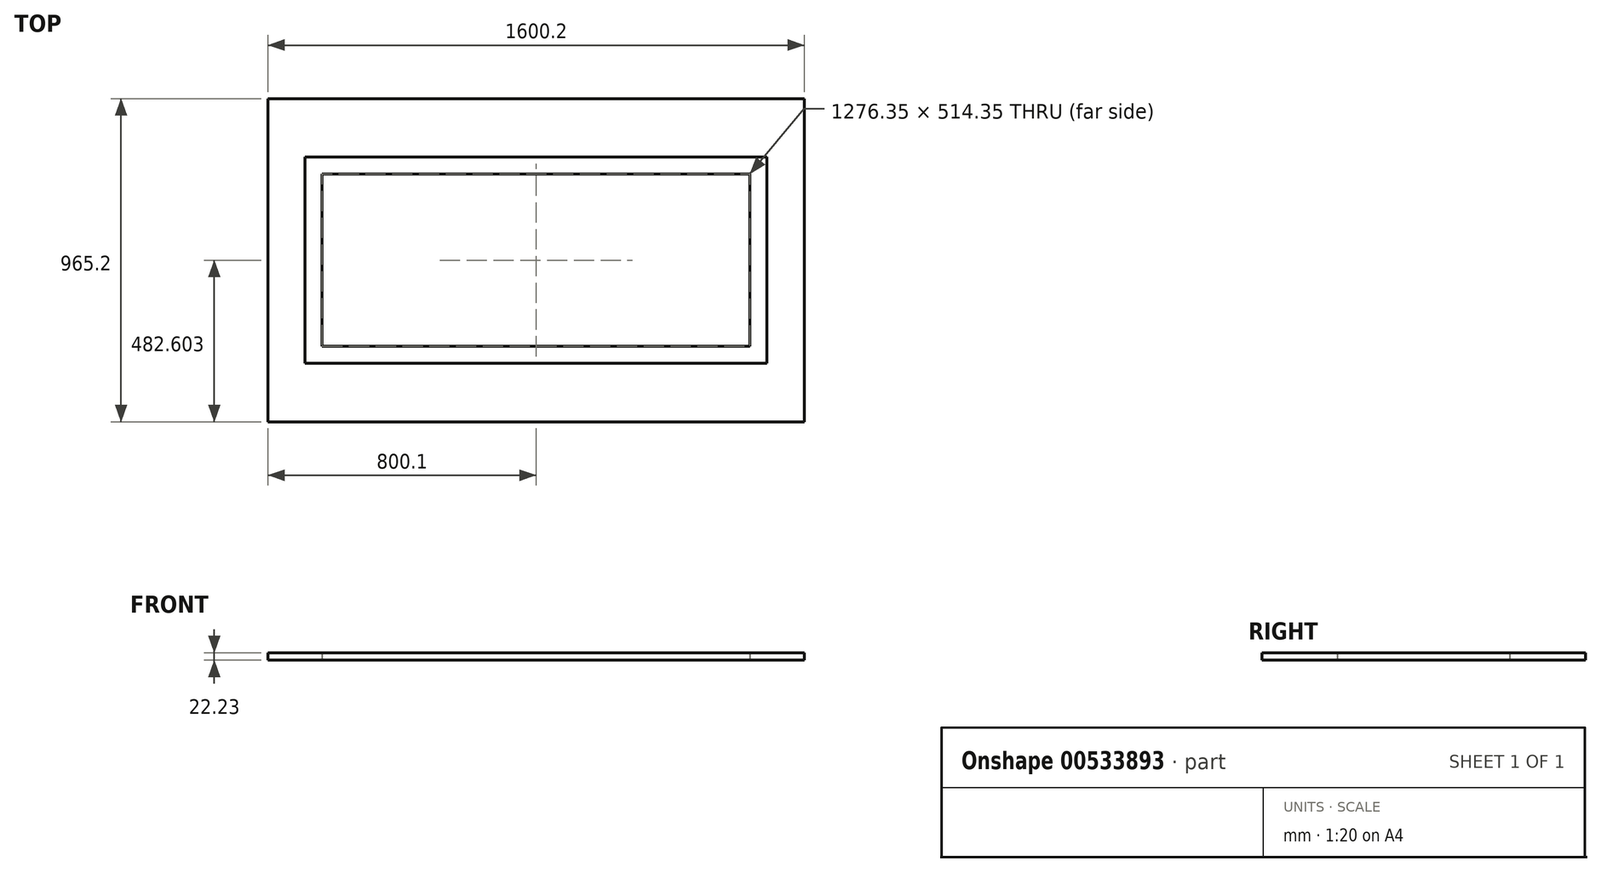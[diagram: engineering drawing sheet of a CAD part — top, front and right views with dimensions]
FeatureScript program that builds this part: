
annotation { "Feature Type Name" : "Feature", "Feature Type Description" : "" }
export const myFeature = defineFeature(function(context is Context, id is Id, definition is map)
    precondition{}
    {
        {
            var Q0;
            Q0=qCreatedBy(makeId("Top.planeOp"),FACE);
            var sketch = newSketch(context, id + "F0", { "sketchPlane" : qUnion([Q0])});
            skLineSegment(sketch, "E0", {"start": v(-545.3, 52.56) * mm, "end": v(-545.3, 1017.76) * mm});
            skLineSegment(sketch, "E1", {"start": v(-545.3, 1017.76) * mm, "end": v(1054.9, 1017.76) * mm});
            skLineSegment(sketch, "E2", {"start": v(-545.3, 52.56) * mm, "end": v(1054.9, 52.56) * mm});
            skLineSegment(sketch, "E3", {"start": v(1054.9, 1017.76) * mm, "end": v(1054.9, 52.56) * mm});
            skPoint(sketch, "E4.middle.positionSnap0", {"position": v(254.8, 1017.76) * mm});
            skPoint(sketch, "E4.middle.positionSnap1", {"position": v(-545.3, 535.16) * mm});
            skPoint(sketch, "E4.centerSnap0", {"position": v(254.8, 1017.76) * mm});
            skPoint(sketch, "E4.centerSnap1", {"position": v(-545.3, 535.16) * mm});
            skLineSegment(sketch, "E5.bottom", {"start": v(-434.18, 227.19) * mm, "end": v(943.77, 227.19) * mm});
            skLineSegment(sketch, "E5.top", {"start": v(-434.18, 843.14) * mm, "end": v(943.77, 843.14) * mm});
            skLineSegment(sketch, "E5.left", {"start": v(-434.18, 227.19) * mm, "end": v(-434.18, 843.14) * mm});
            skLineSegment(sketch, "E5.right", {"start": v(943.77, 227.19) * mm, "end": v(943.77, 843.14) * mm});
            skPoint(sketch, "E5.middle", {"position": v(254.8, 535.16) * mm});
            skLineSegment(sketch, "E6.bottom", {"start": v(-383.38, 277.99) * mm, "end": v(892.97, 277.99) * mm});
            skLineSegment(sketch, "E6.top", {"start": v(-383.38, 792.34) * mm, "end": v(892.97, 792.34) * mm});
            skLineSegment(sketch, "E6.left", {"start": v(-383.38, 277.99) * mm, "end": v(-383.38, 792.34) * mm});
            skLineSegment(sketch, "E6.right", {"start": v(892.97, 277.99) * mm, "end": v(892.97, 792.34) * mm});
            skSolve(sketch);
        }
        {
            var Q0;
            Q0=makeQuery(id+"F0.imprint","IMPRINT",FACE,{"disambiguationData":[TD([[makeQuery(id+"F0.imprint","IMPRINT",EDGE,{"derivedFrom":sQuery(id+"F0.wireOp",EDGE,"E0")}),-1.0]])]});
            extrude(context, id + "F1", {"entities" : qUnion([Q0]), "depth" : 22.22 * mm, "offsetDistance" : 25.4 * mm});
        }
        {
            var Q0;
            Q0=makeQuery(id+"F0.imprint","IMPRINT",FACE,{"disambiguationData":[TD([[makeQuery(id+"F0.imprint","IMPRINT",EDGE,{"derivedFrom":sQuery(id+"F0.wireOp",EDGE,"E5.bottom")}),1.0]])]});
            extrude(context, id + "F2", {"entities" : qUnion([Q0]), "operationType" : NewBodyOperationType.ADD, "depth" : 20.95 * mm, "offsetDistance" : 25.4 * mm});
        }
    });
